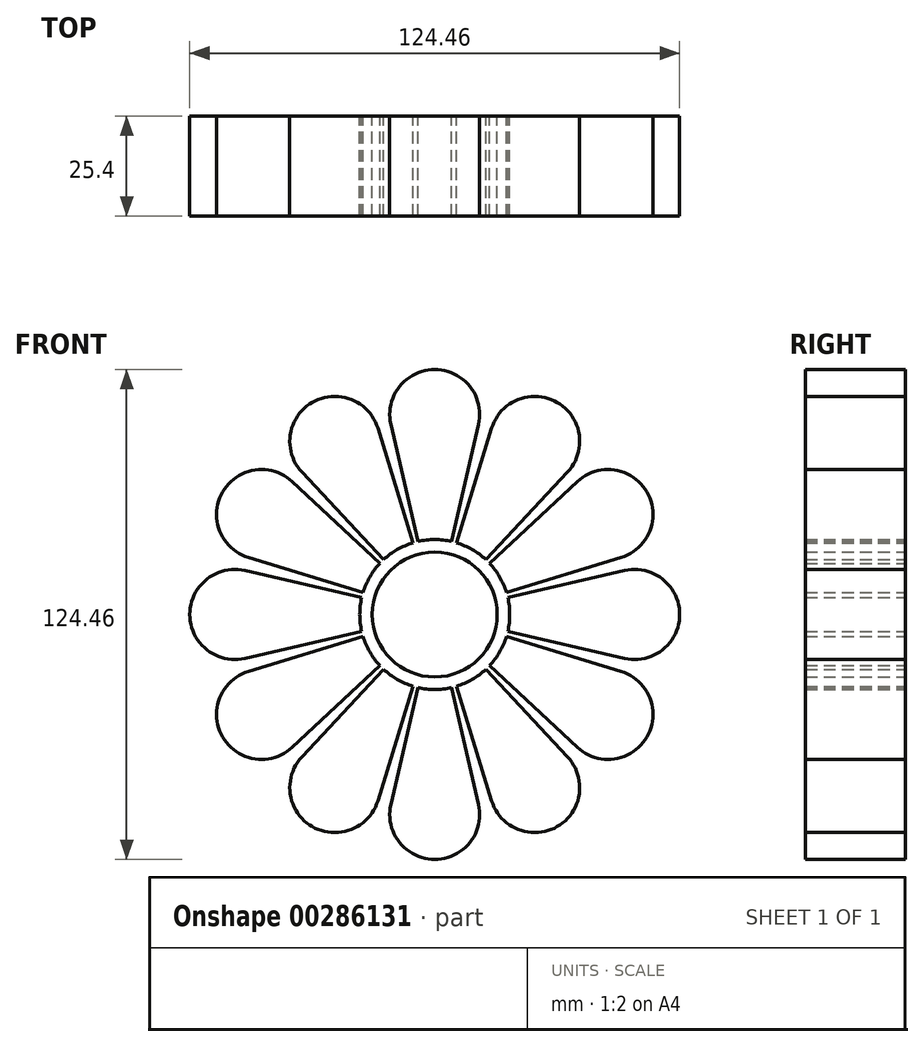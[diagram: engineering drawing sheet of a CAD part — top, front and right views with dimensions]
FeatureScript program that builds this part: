
annotation { "Feature Type Name" : "Feature", "Feature Type Description" : "" }
export const myFeature = defineFeature(function(context is Context, id is Id, definition is map)
    precondition{}
    {
        {
            var Q0;
            Q0=qCreatedBy(makeId("Front.planeOp"),FACE);
            var sketch = newSketch(context, id + "F0", { "sketchPlane" : qUnion([Q0])});
            skArc(sketch, "E0", {"start": v(4.29, 18.56) * mm, "mid": v(0, 19.05) * mm, "end": v(-4.29, 18.56) * mm});
            skArc(sketch, "E1", {"start": v(11.14, 48.23) * mm, "mid": v(0, 62.23) * mm, "end": v(-11.14, 48.23) * mm});
            skLineSegment(sketch, "E2", {"start": v(-4.29, 18.56) * mm, "end": v(-11.14, 48.23) * mm});
            skLineSegment(sketch, "E3", {"start": v(4.29, 18.56) * mm, "end": v(11.14, 48.23) * mm});
            skCircle(sketch, "E4", {"center": v(0, 0) * mm, "radius": 15.88 * mm});
            skLineSegment(sketch, "E5.1.0", {"start": v(-5.57, 18.22) * mm, "end": v(-14.47, 47.34) * mm});
            skLineSegment(sketch, "E5.1.1", {"start": v(-13, 13.93) * mm, "end": v(-33.76, 36.2) * mm});
            skArc(sketch, "E5.1.2", {"start": v(-14.47, 47.34) * mm, "mid": v(-31.11, 53.9) * mm, "end": v(-33.76, 36.2) * mm});
            skArc(sketch, "E5.1.3", {"start": v(-5.57, 18.22) * mm, "mid": v(-9.52, 16.5) * mm, "end": v(-13, 13.93) * mm});
            skLineSegment(sketch, "E5.2.0", {"start": v(-13.93, 13) * mm, "end": v(-36.2, 33.76) * mm});
            skLineSegment(sketch, "E5.2.1", {"start": v(-18.22, 5.57) * mm, "end": v(-47.34, 14.47) * mm});
            skArc(sketch, "E5.2.2", {"start": v(-36.2, 33.76) * mm, "mid": v(-53.9, 31.12) * mm, "end": v(-47.34, 14.47) * mm});
            skArc(sketch, "E5.2.3", {"start": v(-13.93, 13) * mm, "mid": v(-16.5, 9.53) * mm, "end": v(-18.22, 5.57) * mm});
            skLineSegment(sketch, "E6.1.3.0", {"start": v(-18.56, 4.29) * mm, "end": v(-48.23, 11.14) * mm});
            skLineSegment(sketch, "E6.3.3.0", {"start": v(-18.56, -4.29) * mm, "end": v(-48.23, -11.14) * mm});
            skArc(sketch, "E6.6.3.0", {"start": v(-48.23, 11.14) * mm, "mid": v(-62.23, 0) * mm, "end": v(-48.23, -11.14) * mm});
            skArc(sketch, "E6.10.3.0", {"start": v(-18.56, 4.29) * mm, "mid": v(-19.05, 0) * mm, "end": v(-18.56, -4.29) * mm});
            skLineSegment(sketch, "E6.1.4.0", {"start": v(-18.22, -5.57) * mm, "end": v(-47.34, -14.47) * mm});
            skLineSegment(sketch, "E6.3.4.0", {"start": v(-13.93, -13) * mm, "end": v(-36.2, -33.76) * mm});
            skArc(sketch, "E6.6.4.0", {"start": v(-47.34, -14.47) * mm, "mid": v(-53.9, -31.11) * mm, "end": v(-36.2, -33.76) * mm});
            skArc(sketch, "E6.10.4.0", {"start": v(-18.22, -5.57) * mm, "mid": v(-16.5, -9.52) * mm, "end": v(-13.93, -13) * mm});
            skLineSegment(sketch, "E6.1.5.0", {"start": v(-13, -13.93) * mm, "end": v(-33.76, -36.2) * mm});
            skLineSegment(sketch, "E6.3.5.0", {"start": v(-5.57, -18.22) * mm, "end": v(-14.47, -47.34) * mm});
            skArc(sketch, "E6.6.5.0", {"start": v(-33.76, -36.2) * mm, "mid": v(-31.12, -53.9) * mm, "end": v(-14.47, -47.34) * mm});
            skArc(sketch, "E6.10.5.0", {"start": v(-13, -13.93) * mm, "mid": v(-9.53, -16.5) * mm, "end": v(-5.57, -18.22) * mm});
            skLineSegment(sketch, "E6.1.6.0", {"start": v(-4.29, -18.56) * mm, "end": v(-11.14, -48.23) * mm});
            skLineSegment(sketch, "E6.3.6.0", {"start": v(4.29, -18.56) * mm, "end": v(11.14, -48.23) * mm});
            skArc(sketch, "E6.6.6.0", {"start": v(-11.14, -48.23) * mm, "mid": v(0, -62.23) * mm, "end": v(11.14, -48.23) * mm});
            skArc(sketch, "E6.10.6.0", {"start": v(-4.29, -18.56) * mm, "mid": v(0, -19.05) * mm, "end": v(4.29, -18.56) * mm});
            skLineSegment(sketch, "E6.1.7.0", {"start": v(5.57, -18.22) * mm, "end": v(14.47, -47.34) * mm});
            skLineSegment(sketch, "E6.3.7.0", {"start": v(13, -13.93) * mm, "end": v(33.76, -36.2) * mm});
            skArc(sketch, "E6.6.7.0", {"start": v(14.47, -47.34) * mm, "mid": v(31.11, -53.9) * mm, "end": v(33.76, -36.2) * mm});
            skArc(sketch, "E6.10.7.0", {"start": v(5.57, -18.22) * mm, "mid": v(9.52, -16.5) * mm, "end": v(13, -13.93) * mm});
            skLineSegment(sketch, "E6.1.8.0", {"start": v(13.93, -13) * mm, "end": v(36.2, -33.76) * mm});
            skLineSegment(sketch, "E6.3.8.0", {"start": v(18.22, -5.57) * mm, "end": v(47.34, -14.47) * mm});
            skArc(sketch, "E6.6.8.0", {"start": v(36.2, -33.76) * mm, "mid": v(53.9, -31.12) * mm, "end": v(47.34, -14.47) * mm});
            skArc(sketch, "E6.10.8.0", {"start": v(13.93, -13) * mm, "mid": v(16.5, -9.53) * mm, "end": v(18.22, -5.57) * mm});
            skLineSegment(sketch, "E6.1.9.0", {"start": v(18.56, -4.29) * mm, "end": v(48.23, -11.14) * mm});
            skLineSegment(sketch, "E6.3.9.0", {"start": v(18.56, 4.29) * mm, "end": v(48.23, 11.14) * mm});
            skArc(sketch, "E6.6.9.0", {"start": v(48.23, -11.14) * mm, "mid": v(62.23, 0) * mm, "end": v(48.23, 11.14) * mm});
            skArc(sketch, "E6.10.9.0", {"start": v(18.56, -4.29) * mm, "mid": v(19.05, 0) * mm, "end": v(18.56, 4.29) * mm});
            skLineSegment(sketch, "E6.1.10.0", {"start": v(18.22, 5.57) * mm, "end": v(47.34, 14.47) * mm});
            skLineSegment(sketch, "E6.3.10.0", {"start": v(13.93, 13) * mm, "end": v(36.2, 33.76) * mm});
            skArc(sketch, "E6.6.10.0", {"start": v(47.34, 14.47) * mm, "mid": v(53.9, 31.11) * mm, "end": v(36.2, 33.76) * mm});
            skArc(sketch, "E6.10.10.0", {"start": v(18.22, 5.57) * mm, "mid": v(16.5, 9.52) * mm, "end": v(13.93, 13) * mm});
            skLineSegment(sketch, "E6.1.11.0", {"start": v(13, 13.93) * mm, "end": v(33.76, 36.2) * mm});
            skLineSegment(sketch, "E6.3.11.0", {"start": v(5.57, 18.22) * mm, "end": v(14.47, 47.34) * mm});
            skArc(sketch, "E6.6.11.0", {"start": v(33.76, 36.2) * mm, "mid": v(31.11, 53.9) * mm, "end": v(14.47, 47.34) * mm});
            skArc(sketch, "E6.10.11.0", {"start": v(13, 13.93) * mm, "mid": v(9.53, 16.5) * mm, "end": v(5.57, 18.22) * mm});
            skSolve(sketch);
        }
        {
            var Q0;
            Q0 = qSketchRegion(id + "F0", true);
            extrude(context, id + "F1", {"entities" : qUnion([Q0]), "depth" : 25.4 * mm});
        }
    });
